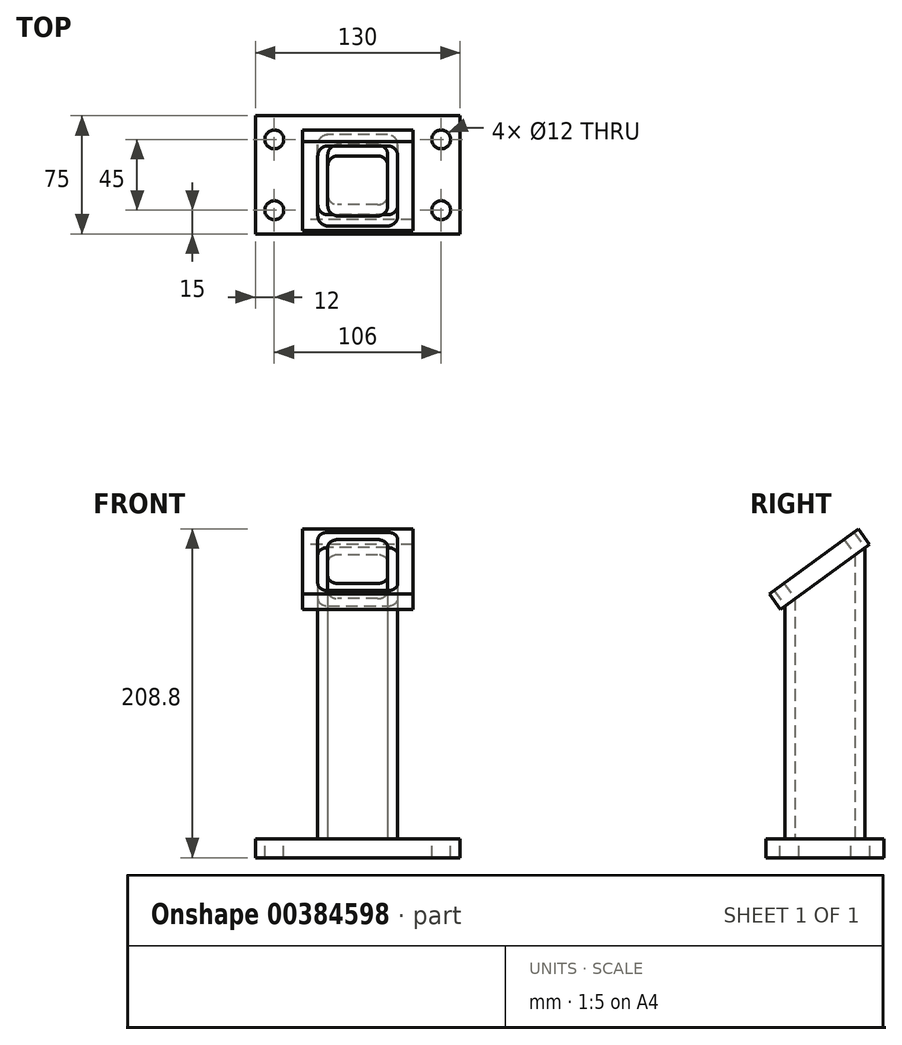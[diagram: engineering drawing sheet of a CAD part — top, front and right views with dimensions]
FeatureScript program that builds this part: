
annotation { "Feature Type Name" : "Feature", "Feature Type Description" : "" }
export const myFeature = defineFeature(function(context is Context, id is Id, definition is map)
    precondition{}
    {
        {
            var Q0;
            Q0=qCreatedBy(makeId("Top.planeOp"),FACE);
            var sketch = newSketch(context, id + "F0", { "sketchPlane" : qUnion([Q0])});
            skLineSegment(sketch, "E0.bottom", {"start": v(65, 37.5) * mm, "end": v(-65, 37.5) * mm});
            skLineSegment(sketch, "E0.top", {"start": v(65, -37.5) * mm, "end": v(-65, -37.5) * mm});
            skLineSegment(sketch, "E0.left", {"start": v(65, 37.5) * mm, "end": v(65, -37.5) * mm});
            skLineSegment(sketch, "E0.right", {"start": v(-65, 37.5) * mm, "end": v(-65, -37.5) * mm});
            skPoint(sketch, "E0.middle", {"position": v(0, 0) * mm});
            skSolve(sketch);
        }
        {
            var Q0;
            Q0=makeQuery(id+"F0.imprint","IMPRINT",FACE,{"disambiguationData":[TD([[makeQuery(id+"F0.imprint","IMPRINT",EDGE,{"derivedFrom":sQuery(id+"F0.wireOp",EDGE,"E0.bottom")}),1.0]])]});
            extrude(context, id + "F1", {"entities" : qUnion([Q0]), "depth" : -12 * mm});
        }
        {
            var Q0;
            Q0=makeQuery(id+"F1.opExtrude","CAP_FACE",FACE,{"disambiguationData":[OSD([sQuery(id+"F0.wireOp",EDGE,"E0.bottom"),sQuery(id+"F0.wireOp",EDGE,"E0.top"),sQuery(id+"F0.wireOp",EDGE,"E0.left"),sQuery(id+"F0.wireOp",EDGE,"E0.right")])],"isStart":true});
            var sketch = newSketch(context, id + "F2", { "sketchPlane" : qUnion([Q0])});
            skLineSegment(sketch, "E1.bottom", {"start": v(19.05, -25.4) * mm, "end": v(-19.05, -25.4) * mm});
            skLineSegment(sketch, "E1.top", {"start": v(19.05, 25.4) * mm, "end": v(-19.05, 25.4) * mm});
            skLineSegment(sketch, "E1.left", {"start": v(25.4, -19.05) * mm, "end": v(25.4, 19.05) * mm});
            skLineSegment(sketch, "E1.right", {"start": v(-25.4, -19.05) * mm, "end": v(-25.4, 19.05) * mm});
            skPoint(sketch, "E1.middle", {"position": v(0, 0) * mm});
            skPoint(sketch, "E2.visualSharp", {"position": v(-25.4, -25.4) * mm});
            skArc(sketch, "E2.filletArc", {"start": v(-25.4, -19.05) * mm, "mid": v(-23.54, -23.54) * mm, "end": v(-19.05, -25.4) * mm});
            skPoint(sketch, "E3.visualSharp", {"position": v(-25.4, 25.4) * mm});
            skArc(sketch, "E3.filletArc", {"start": v(-19.05, 25.4) * mm, "mid": v(-23.54, 23.54) * mm, "end": v(-25.4, 19.05) * mm});
            skPoint(sketch, "E4.visualSharp", {"position": v(25.4, 25.4) * mm});
            skArc(sketch, "E4.filletArc", {"start": v(25.4, 19.05) * mm, "mid": v(23.54, 23.54) * mm, "end": v(19.05, 25.4) * mm});
            skPoint(sketch, "E5.visualSharp", {"position": v(25.4, -25.4) * mm});
            skArc(sketch, "E5.filletArc", {"start": v(19.05, -25.4) * mm, "mid": v(23.54, -23.54) * mm, "end": v(25.4, -19.05) * mm});
            skLineSegment(sketch, "E6.bottom", {"start": v(12.7, 19.05) * mm, "end": v(-12.7, 19.05) * mm});
            skLineSegment(sketch, "E6.top", {"start": v(12.7, -19.05) * mm, "end": v(-12.7, -19.05) * mm});
            skLineSegment(sketch, "E6.left", {"start": v(19.05, 12.7) * mm, "end": v(19.05, -12.7) * mm});
            skLineSegment(sketch, "E6.right", {"start": v(-19.05, 12.7) * mm, "end": v(-19.05, -12.7) * mm});
            skArc(sketch, "E7.filletArc", {"start": v(-12.7, 19.05) * mm, "mid": v(-17.2, 17.2) * mm, "end": v(-19.05, 12.7) * mm});
            skArc(sketch, "E8.filletArc", {"start": v(19.05, 12.7) * mm, "mid": v(17.2, 17.2) * mm, "end": v(12.7, 19.05) * mm});
            skArc(sketch, "E9.filletArc", {"start": v(12.7, -19.05) * mm, "mid": v(17.2, -17.2) * mm, "end": v(19.05, -12.7) * mm});
            skArc(sketch, "E10.filletArc", {"start": v(-19.05, -12.7) * mm, "mid": v(-17.2, -17.2) * mm, "end": v(-12.7, -19.05) * mm});
            skSolve(sketch);
        }
        {
            var Q0;
            Q0=qSketchRegion(id+"F2",true);
            extrude(context, id + "F3", {"entities" : qUnion([Q0]), "operationType" : NewBodyOperationType.ADD, "depth" : 185 * mm});
        }
        {
            var Q0;
            {var subQ0=sQuery(id+"F0.wireOp",EDGE,"E0.left");var subQ1=sQuery(id+"F0.wireOp",EDGE,"E0.bottom");var subQ2=sQuery(id+"F0.wireOp",EDGE,"E0.right");var subQ3=sQuery(id+"F0.wireOp",EDGE,"E0.top");Q0=makeQuery(id+"F3.boolean.opBoolean","SPLIT",FACE,{"disambiguationData":[TD([makeQuery(id+"F1.opExtrude","SWEPT_FACE",FACE,{"disambiguationData":[OSD([subQ1])]})])],"derivedFrom":makeQuery(id+"F1.opExtrude","CAP_FACE",FACE,{"disambiguationData":[OSD([subQ1,subQ3,subQ0,subQ2])],"isStart":true})});}
            var sketch = newSketch(context, id + "F4", { "sketchPlane" : qUnion([Q0])});
            skLineSegment(sketch, "E11", {"start": v(-65, -37.5) * mm, "end": v(-53, -37.5) * mm, "construction": true});
            skLineSegment(sketch, "E12", {"start": v(-53, -37.5) * mm, "end": v(-53, -22.5) * mm, "construction": true});
            skLineSegment(sketch, "E13", {"start": v(-65, 37.5) * mm, "end": v(-53, 37.5) * mm, "construction": true});
            skLineSegment(sketch, "E14", {"start": v(-53, 37.5) * mm, "end": v(-53, 22.5) * mm, "construction": true});
            skLineSegment(sketch, "E15", {"start": v(65, 37.5) * mm, "end": v(53, 37.5) * mm, "construction": true});
            skLineSegment(sketch, "E16", {"start": v(65, -37.5) * mm, "end": v(53, -37.5) * mm, "construction": true});
            skLineSegment(sketch, "E17", {"start": v(53, -37.5) * mm, "end": v(53, -22.5) * mm, "construction": true});
            skLineSegment(sketch, "E18", {"start": v(53, 37.5) * mm, "end": v(53, 22.5) * mm, "construction": true});
            skSolve(sketch);
        }
        {
            var Q0;
            Q0=sQuery(id+"F4.wireOp",VERTEX,"E14.end");
            var Q1;
            Q1=sQuery(id+"F4.wireOp",VERTEX,"E18.end");
            var Q2;
            Q2=sQuery(id+"F4.wireOp",VERTEX,"E17.end");
            var Q3;
            Q3=sQuery(id+"F4.wireOp",VERTEX,"E12.end");
            var Q4;
            Q4=makeQuery(id+"F1.opExtrude","SWEPT_BODY",BODY,{"disambiguationData":[OSD([sQuery(id+"F0.wireOp",EDGE,"E0.bottom"),sQuery(id+"F0.wireOp",EDGE,"E0.top"),sQuery(id+"F0.wireOp",EDGE,"E0.left"),sQuery(id+"F0.wireOp",EDGE,"E0.right")])]});
            hole(context, id + "F5", {"style" : HoleStyle.SIMPLE, "endStyle" : HoleEndStyle.THROUGH, "holeDiameter" : 12 * mm, "isTappedThrough" : true, "tappedDepth" : 12 * mm, "tapClearance" : 3, "locations" : qUnion([Q0, Q1, Q2, Q3]), "scope" : qUnion([Q4])});
        }
        {
            var Q0;
            Q0=makeQuery(id+"F3.opExtrude","SWEPT_FACE",FACE,{"disambiguationData":[OSD([sQuery(id+"F2.wireOp",EDGE,"E1.left")])]});
            var sketch = newSketch(context, id + "F6", { "sketchPlane" : qUnion([Q0])});
            skLineSegment(sketch, "E19", {"start": v(-19.05, 185) * mm, "end": v(-25.4, 185) * mm, "construction": true});
            skLineSegment(sketch, "E20", {"start": v(-25.4, 185) * mm, "end": v(25.4, 185) * mm});
            skLineSegment(sketch, "E21", {"start": v(25.4, 185) * mm, "end": v(-25.4, 147.96) * mm});
            skLineSegment(sketch, "E22", {"start": v(-25.4, 185) * mm, "end": v(-25.4, 147.96) * mm});
            skSolve(sketch);
        }
        {
            var Q0;
            Q0 = qSketchRegion(id + "F6", true);
            extrude(context, id + "F7", {"entities" : qUnion([Q0]), "operationType" : NewBodyOperationType.REMOVE, "oppositeDirection" : true, "depth" : 50.8 * mm});
        }
        {
            var Q0;
            Q0=makeQuery(id+"F7.boolean.opBoolean","COPY",FACE,{"derivedFrom":makeQuery(id+"F7.opExtrude","SWEPT_FACE",FACE,{"disambiguationData":[OSD([sQuery(id+"F6.wireOp",EDGE,"E21")])]})});
            var sketch = newSketch(context, id + "F8", { "sketchPlane" : qUnion([Q0])});
            skLineSegment(sketch, "E23.bottom", {"start": v(35, 133.09) * mm, "end": v(-35, 133.09) * mm});
            skLineSegment(sketch, "E23.top", {"start": v(35, 63.09) * mm, "end": v(-35, 63.09) * mm});
            skLineSegment(sketch, "E23.left", {"start": v(35, 133.09) * mm, "end": v(35, 63.09) * mm});
            skLineSegment(sketch, "E23.right", {"start": v(-35, 133.09) * mm, "end": v(-35, 63.09) * mm});
            skPoint(sketch, "E23.middle", {"position": v(0, 98.09) * mm});
            skPoint(sketch, "E23.middle.positionSnap0", {"position": v(0, 121.67) * mm});
            skPoint(sketch, "E23.middle.positionSnap1", {"position": v(-19.05, 98.09) * mm});
            skPoint(sketch, "E23.centerSnap0", {"position": v(0, 121.67) * mm});
            skPoint(sketch, "E23.centerSnap1", {"position": v(-19.05, 98.09) * mm});
            skSolve(sketch);
        }
        {
            var Q0;
            Q0=makeQuery(id+"F8.imprint","IMPRINT",FACE,{"disambiguationData":[TD([[makeQuery(id+"F8.imprint","IMPRINT",EDGE,{"derivedFrom":sQuery(id+"F8.wireOp",EDGE,"E23.bottom")}),1.0]])]});
            var Q1;
            {var subQ0=makeQuery(id+"F7.opExtrude","SWEPT_FACE",FACE,{"disambiguationData":[OSD([sQuery(id+"F6.wireOp",EDGE,"E21")])]});Q1=makeQuery(id+"F8.imprint","IMPRINT",FACE,{"disambiguationData":[TD([[makeQuery(id+"F8.imprint","IMPRINT",EDGE,{"derivedFrom":makeQuery(id+"F7.boolean.opBoolean","INTERSECT",EDGE,{"derivedFrom":[makeQuery(id+"F3.opExtrude","SWEPT_FACE",FACE,{"disambiguationData":[OSD([sQuery(id+"F2.wireOp",EDGE,"E6.bottom")])]}),subQ0]})}),1.0]])]});}
            var Q2;
            {var subQ0=sQuery(id+"F6.wireOp",EDGE,"E21");Q2=makeQuery(id+"F8.imprint","IMPRINT",FACE,{"disambiguationData":[TD([[makeQuery(id+"F8.imprint","IMPRINT",EDGE,{"derivedFrom":makeQuery(id+"F7.boolean.opBoolean","COPY",EDGE,{"derivedFrom":makeQuery(id+"F7.opExtrude","CAP_EDGE",EDGE,{"disambiguationData":[OSD([subQ0])],"isStart":true})})}),-1.0]])]});}
            extrude(context, id + "F9", {"entities" : qUnion([Q0, Q1, Q2]), "operationType" : NewBodyOperationType.ADD, "depth" : 12 * mm});
        }
    });
